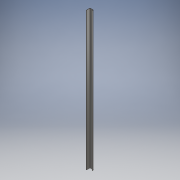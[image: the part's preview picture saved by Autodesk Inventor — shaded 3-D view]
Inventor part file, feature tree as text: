
AUTODESK INVENTOR PART (.ipt)
format: ipt  version: 2017 (Build 210142000, 142)  size: 137,216 bytes
history: native  units: mm
features: sheet_metal_op x3, other x2, sketch x1
ambient origin geometry x8: Origin, YZ Plane, XZ Plane, XY Plane, X Axis, Y Axis, Z Axis, Center Point
bodies: Solid1 (feature_tree)
feature tree (6):
  sheet_metal_op  "Contour Flange1"
  sketch  "Sketch1"  dims[d0=25.0mm d1=25.0mm d2=10.0mm d3=1.5mm d4=0.75mm d5=3.0mm d6=1.5mm d7=930.0mm d8=1.5mm d9=0.5mm d10=6.0mm d11=1.5mm d12=1.5mm]
  other  "Plate1"
  sheet_metal_op  "Bend1"
  sheet_metal_op  "Corner1"
  other  "Definition1"
